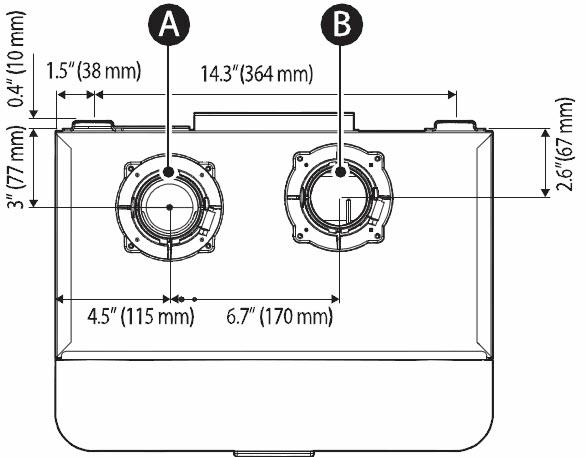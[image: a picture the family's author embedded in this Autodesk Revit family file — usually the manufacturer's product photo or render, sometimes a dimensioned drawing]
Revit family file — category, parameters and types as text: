
# Revit family: Water_Heater-Racks-Navien-NPE-9_Unit_Front---
name_source: partatom
category: Mechanical Equipment
revit_build: Autodesk Revit 2016 (Build: 20150220_1215(x64)
units: mm (PartAtom-declared; Revit-internal decimal feet)

## family parameters
Cut with Voids When Loaded = No
Host = Face
OmniClass Number = 23.65.35.11
OmniClass Title = Supply Water Heaters
Part Type = Normal
Room Calculation Point = No
Round Connector Dimension = Use Diameter
Shared = No

## types (4) — shared parameters
2" Exhaust/Intake = Yes
3" Exhaust/Intake = No
Apparent Load = 0 VA
Assembly Code = D3010500
Certifications = Energy Star | AHRI | CSA | CSA | NFS
Cold Water Inlet = 1"
Configuration = NPE_F9_3F2F_4F
Default Elevation = 48 "
Depth = 23.8 "
Description = 9 Unit Front
Exhaust = 2"
Finish = Metal - Navien - White
Flow Rate = 1 GPM
Flow Rate Note = 35°F (19°C) temp rise: 11.2 GPM (42 L/m) | 45°F (25°C) temp rise: 8.7 GPM (33 L/m) | 67°F (36°C) temp rise: NPE-240A: 5.6 GPM(21 L/m), NPE-240S: 5.7 GPM(22 L/m)
Frequency = 60 Hz
Gas Inlet = 1"
Heating Capacity = 120000.0 Btu/h
Heating Capacity Note = 19,900–199,900 (BTU/H)
Height = 65.5 "
Hot Water Outlet = 1"
Ignition = Electronic ignition
Installation Type = Indoor
Intake = 2"
Keynote = 22 33 00.A1
Manifold(s) = (1) 30019040A + (1) 30019041A + (1) 30019043A
Manufacturer = Navien, Inc.
Manufacturer Fax Number = (949) 420-0430
Natural Gas Manifold Pressure = -0.05" WC to -0.58" WC
Natural Gas Supply Pressure = 3.5"–10.5" WC
Number of Poles = 1
Phase = 1
Power Factor = 1
Product Documentation Link = https://www.navieninc.com
Product Name = NPE Series Tankless Water Heaters w/ Racks
Product Page URL = https://www.navieninc.com
Propane Gas Manifold Pressure = -0.10" WC to -0.78" WC
Propane Gas Supply Pressure = 8"–13" WC
Rack(s) = (2) GFFM-KDIZUS-003 + (7) GFFM-KDIZUS-004
Required Cascade Operation Accessory = (9) 30014367A (Common Vent Damper & Cascade Communication Cable) or (8) GXXX000546 (Individual Vent Cascade Communication Cable)
URL = https://www.navieninc.com
Venting = Exhaust: 2" PVC, CPVC, PP, SS / 2" special gas vent type BH (Class II, A/B/C) | Intake: 2" PVC, CPVC, PP, SS / 2" special gas vent type BH (Class II, A/B/C) | Vent clearances: 0" to combustibles
Venting Type = Forced draft direct vent
Version = 2016 - v1.0.a
Voltage = 120 V
Water Pressure = 15–150 PSI
Wi-Fi Ready = NaviLink Wi-Fi Control: PBCM-AS-001
Width = 23.3 "

## per-type parameters (varying)
| type | Constraints | Model | Natural Gas | Propane Gas | Recirculation Inlet | Recirculation Inlet Visibility | Tankless Water Heaters | Weight |
| Natural Gas - Recirculating System - NPE-240A(Advanced)-NG | 6 | (9) NPE-240A-NG | Yes | No | 0" | Yes | (9) NPE-240A-NG | 82.00 lbf |
| Natural Gas - NPE-240S(Standard)-NG | 7 | (9) NPE-240S-NG | Yes | No | 1" | No | (9) NPE-240S-NG | 75.00 lbf |
| Propane Gas - Recirculating System - NPE-240A(Advanced)-LPG | 6 | (9) NPE-240A-LPG | No | Yes | 0" | Yes | (9) NPE-240A-LPG | 82.00 lbf |
| Propane Gas - NPE-240S(Standard)-LPG | 7 | (9) NPE-240S-LPG | No | Yes | 1" | No | (9) NPE-240S-LPG | 75.00 lbf |

## geometry (parser evidence)
native form markers: Sweep x21
no freeform markers — native parametric forms only
